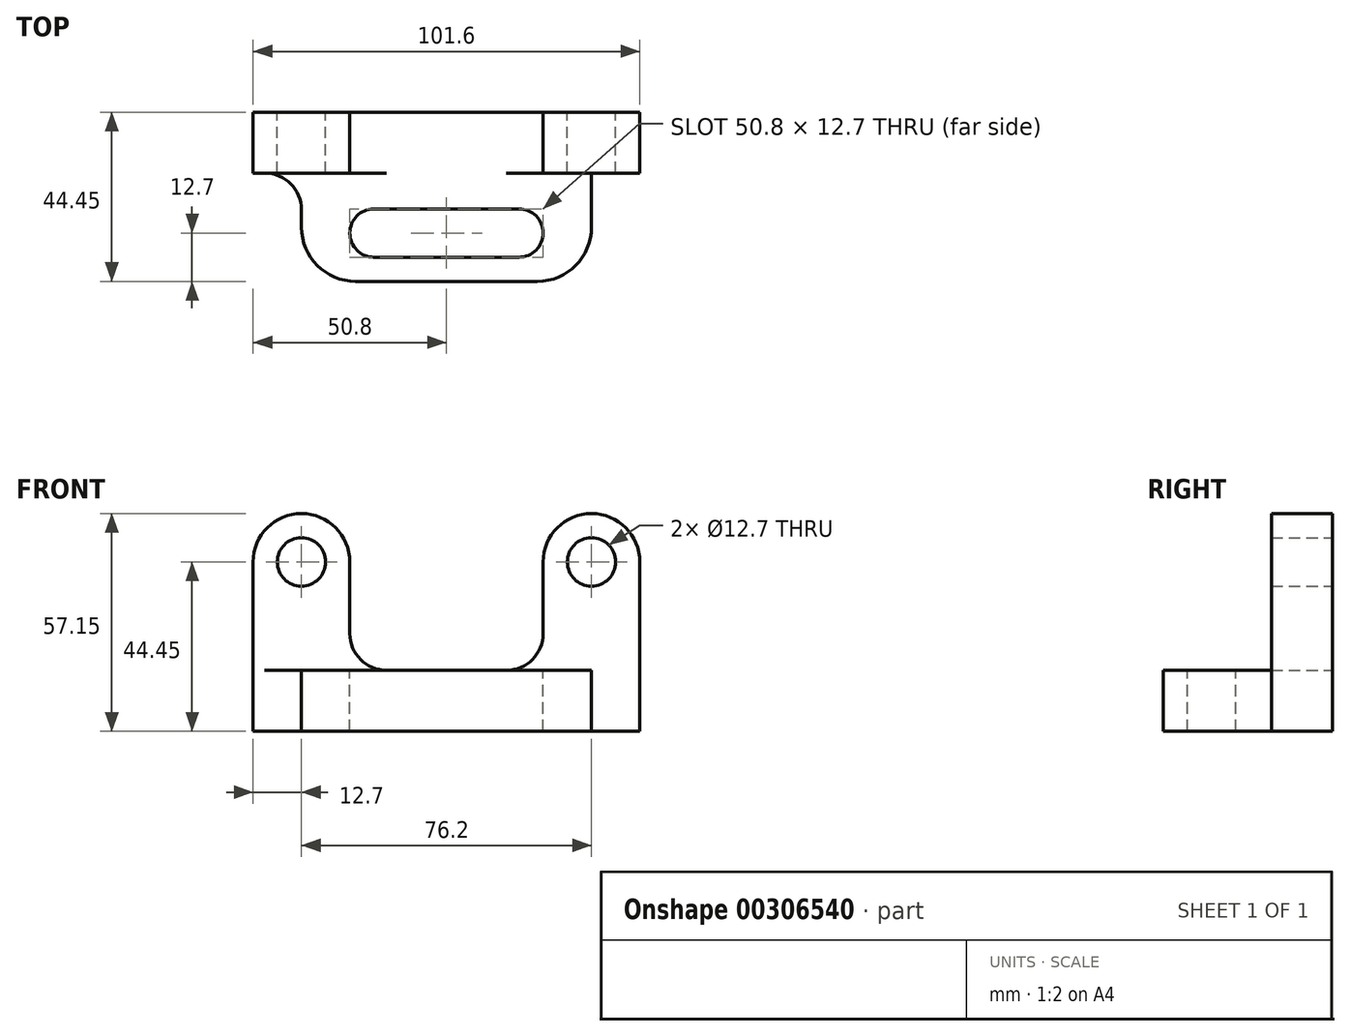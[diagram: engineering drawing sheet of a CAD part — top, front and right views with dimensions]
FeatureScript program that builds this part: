
annotation { "Feature Type Name" : "Feature", "Feature Type Description" : "" }
export const myFeature = defineFeature(function(context is Context, id is Id, definition is map)
    precondition{}
    {
        {
            var Q0;
            Q0=qCreatedBy(makeId("Front.planeOp"),FACE);
            var sketch = newSketch(context, id + "F0", { "sketchPlane" : qUnion([Q0])});
            skCircle(sketch, "E0", {"center": v(12.7, 44.45) * mm, "radius": 6.35 * mm});
            skCircle(sketch, "E1", {"center": v(88.9, 44.45) * mm, "radius": 6.35 * mm});
            skArc(sketch, "E2", {"start": v(0, 44.45) * mm, "mid": v(12.7, 57.15) * mm, "end": v(25.4, 44.45) * mm});
            skArc(sketch, "E3", {"start": v(76.2, 44.45) * mm, "mid": v(88.9, 57.15) * mm, "end": v(101.6, 44.45) * mm});
            skLineSegment(sketch, "E4", {"start": v(0, 44.45) * mm, "end": v(0, 0) * mm});
            skLineSegment(sketch, "E5", {"start": v(0, 0) * mm, "end": v(101.6, 0) * mm});
            skLineSegment(sketch, "E6", {"start": v(101.6, 0) * mm, "end": v(101.6, 44.45) * mm});
            skLineSegment(sketch, "E7", {"start": v(25.4, 44.45) * mm, "end": v(25.4, 16) * mm});
            skLineSegment(sketch, "E8", {"start": v(25.4, 16) * mm, "end": v(76.2, 16) * mm});
            skLineSegment(sketch, "E9", {"start": v(76.2, 16) * mm, "end": v(76.2, 44.45) * mm});
            skSolve(sketch);
        }
        {
            var Q0;
            Q0 = qSketchRegion(id + "F0", true);
            extrude(context, id + "F1", {"entities" : qUnion([Q0]), "depth" : 16 * mm});
        }
        {
            var Q0;
            Q0=makeQuery(id+"F1.opExtrude","SWEPT_EDGE",EDGE,{"disambiguationData":[OSD([sQuery(id+"F0.wireOp",EDGE,"E7"),sQuery(id+"F0.wireOp",EDGE,"E8")])]});
            var Q1;
            Q1=makeQuery(id+"F1.opExtrude","SWEPT_EDGE",EDGE,{"disambiguationData":[OSD([sQuery(id+"F0.wireOp",EDGE,"E8"),sQuery(id+"F0.wireOp",EDGE,"E9")])]});
            fillet(context, id + "F2", {"entities" : qUnion([Q0, Q1]), "radius" : 9.65 * mm, "tangentPropagation" : true, "allowEdgeOverflow" : false});
        }
        {
            var Q0;
            Q0=qCreatedBy(makeId("Top.planeOp"),FACE);
            var sketch = newSketch(context, id + "F3", { "sketchPlane" : qUnion([Q0])});
            skLineSegment(sketch, "E10", {"start": v(12.7, -16) * mm, "end": v(12.7, -44.45) * mm});
            skLineSegment(sketch, "E11", {"start": v(12.7, -44.45) * mm, "end": v(88.9, -44.45) * mm});
            skLineSegment(sketch, "E12", {"start": v(88.9, -44.45) * mm, "end": v(88.9, -16) * mm});
            skLineSegment(sketch, "E13", {"start": v(88.9, -16) * mm, "end": v(12.7, -16) * mm});
            skSolve(sketch);
        }
        {
            var Q0;
            Q0 = qSketchRegion(id + "F3", true);
            extrude(context, id + "F4", {"entities" : qUnion([Q0]), "operationType" : NewBodyOperationType.ADD, "depth" : 16 * mm});
        }
        {
            var Q0;
            Q0=makeQuery(id+"F4.opExtrude","SWEPT_EDGE",EDGE,{"disambiguationData":[OSD([sQuery(id+"F3.wireOp",EDGE,"E10"),sQuery(id+"F3.wireOp",EDGE,"E13")])]});
            var Q1;
            Q1=makeQuery(id+"F4.opExtrude","SWEPT_EDGE",EDGE,{"disambiguationData":[OSD([sQuery(id+"F3.wireOp",EDGE,"E12"),sQuery(id+"F3.wireOp",EDGE,"E13")])]});
            fillet(context, id + "F5", {"entities" : qUnion([Q0, Q1]), "radius" : 9.65 * mm, "tangentPropagation" : true, "allowEdgeOverflow" : false});
        }
        {
            var Q0;
            Q0=makeQuery(id+"F4.opExtrude","SWEPT_EDGE",EDGE,{"disambiguationData":[OSD([sQuery(id+"F3.wireOp",EDGE,"E10"),sQuery(id+"F3.wireOp",EDGE,"E11")])]});
            var Q1;
            Q1=makeQuery(id+"F4.opExtrude","SWEPT_EDGE",EDGE,{"disambiguationData":[OSD([sQuery(id+"F3.wireOp",EDGE,"E11"),sQuery(id+"F3.wireOp",EDGE,"E12")])]});
            fillet(context, id + "F6", {"entities" : qUnion([Q0, Q1]), "radius" : 14.22 * mm, "tangentPropagation" : true, "allowEdgeOverflow" : false});
        }
        {
            var Q0;
            Q0=makeQuery(id+"F4.boolean.opBoolean","MERGE",FACE,{"derivedFrom":[makeQuery(id+"F1.opExtrude","SWEPT_FACE",FACE,{"disambiguationData":[OSD([sQuery(id+"F0.wireOp",EDGE,"E8")])]}),makeQuery(id+"F4.opExtrude","CAP_FACE",FACE,{"disambiguationData":[OSD([sQuery(id+"F3.wireOp",EDGE,"E10"),sQuery(id+"F3.wireOp",EDGE,"E11"),sQuery(id+"F3.wireOp",EDGE,"E12"),sQuery(id+"F3.wireOp",EDGE,"E13")])],"isStart":false})]});
            var sketch = newSketch(context, id + "F7", { "sketchPlane" : qUnion([Q0])});
            skLineSegment(sketch, "E14", {"start": v(0, -31.75) * mm, "end": v(122.21, -31.75) * mm, "construction": true});
            skArc(sketch, "E15", {"start": v(31.75, -25.4) * mm, "mid": v(25.4, -31.75) * mm, "end": v(31.75, -38.1) * mm});
            skArc(sketch, "E16", {"start": v(69.85, -25.4) * mm, "mid": v(76.2, -31.75) * mm, "end": v(69.85, -38.1) * mm});
            skLineSegment(sketch, "E17", {"start": v(31.75, -25.4) * mm, "end": v(69.85, -25.4) * mm});
            skLineSegment(sketch, "E18", {"start": v(31.75, -38.1) * mm, "end": v(69.85, -38.1) * mm});
            skSolve(sketch);
        }
        {
            var Q0;
            Q0 = qSketchRegion(id + "F7", true);
            extrude(context, id + "F8", {"entities" : qUnion([Q0]), "operationType" : NewBodyOperationType.REMOVE, "endBound" : BoundingType.THROUGH_ALL, "oppositeDirection" : true, "depth" : 25.4 * mm});
        }
    });
